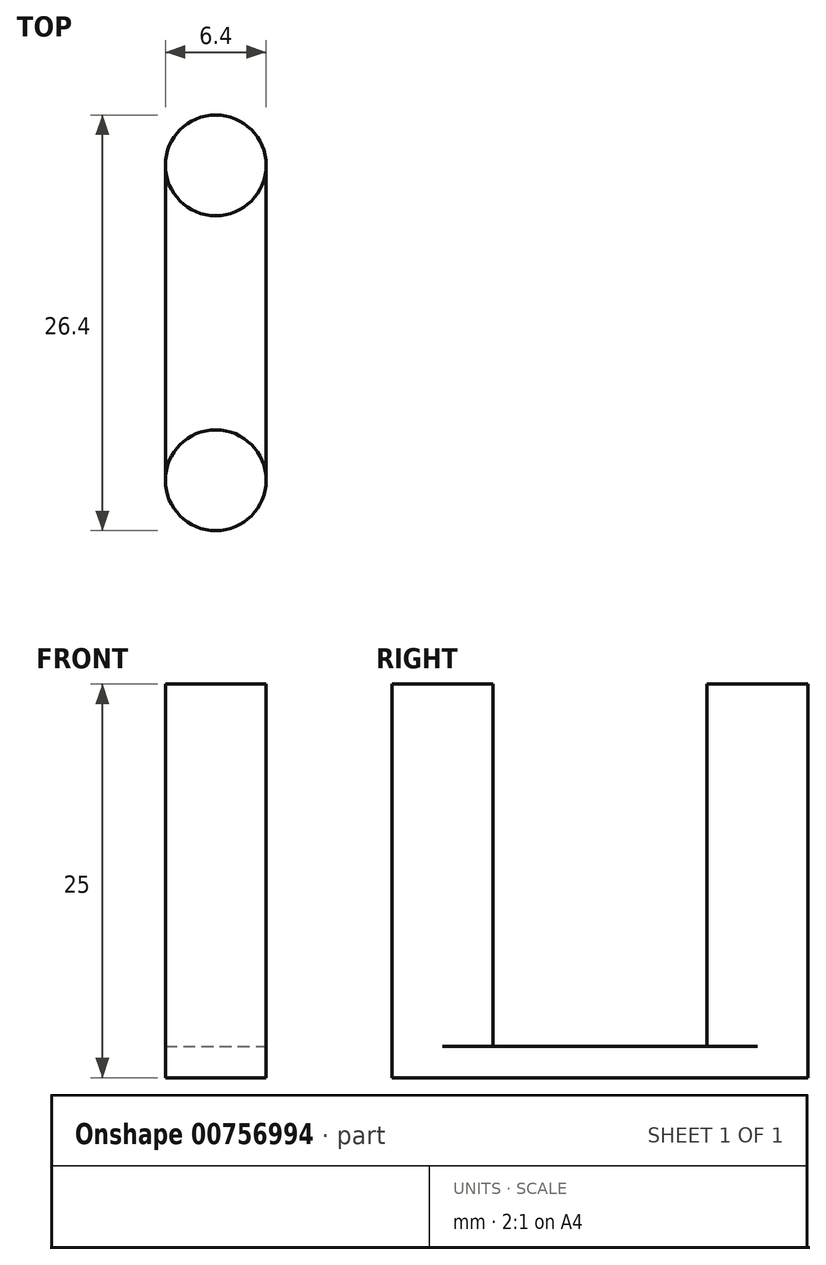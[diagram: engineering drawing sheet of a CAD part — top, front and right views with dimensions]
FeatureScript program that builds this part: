
annotation { "Feature Type Name" : "Feature", "Feature Type Description" : "" }
export const myFeature = defineFeature(function(context is Context, id is Id, definition is map)
    precondition{}
    {
        {
            var Q0;
            Q0=qCreatedBy(makeId("Top.planeOp"),FACE);
            var sketch = newSketch(context, id + "F0", { "sketchPlane" : qUnion([Q0])});
            skCircle(sketch, "E0", {"center": v(0, 0) * mm, "radius": 3.2 * mm});
            skPoint(sketch, "E0.centerSnap0", {"position": v(0, 0) * mm});
            skCircle(sketch, "E1", {"center": v(0, -20) * mm, "radius": 3.2 * mm});
            skLineSegment(sketch, "E2", {"start": v(0, 0) * mm, "end": v(0, -20) * mm, "construction": true});
            skLineSegment(sketch, "E3", {"start": v(3.2, -20) * mm, "end": v(3.2, 0) * mm});
            skLineSegment(sketch, "E4", {"start": v(-3.2, -20) * mm, "end": v(-3.2, 0) * mm});
            skPoint(sketch, "E5.start.orphan", {"position": v(0, -10) * mm});
            skSolve(sketch);
        }
        {
            var Q0;
            {var subQ0=sQuery(id+"F0.wireOp",EDGE,"E1");var subQ1=makeQuery(id+"F0.imprint","INTERSECT",VERTEX,{"derivedFrom":[subQ0,sQuery(id+"F0.wireOp",EDGE,"E3")]});Q0=makeQuery(id+"F0.imprint","IMPRINT",FACE,{"disambiguationData":[TD([[makeQuery(id+"F0.imprint","IMPRINT",EDGE,{"disambiguationData":[TD([[subQ1,-1.0]])],"derivedFrom":subQ0}),1.0]])]});}
            var Q1;
            {var subQ0=sQuery(id+"F0.wireOp",EDGE,"E0");var subQ1=makeQuery(id+"F0.imprint","INTERSECT",VERTEX,{"derivedFrom":[subQ0,sQuery(id+"F0.wireOp",EDGE,"E3")]});Q1=makeQuery(id+"F0.imprint","IMPRINT",FACE,{"disambiguationData":[TD([[makeQuery(id+"F0.imprint","IMPRINT",EDGE,{"disambiguationData":[TD([[subQ1,-1.0]])],"derivedFrom":subQ0}),1.0]])]});}
            extrude(context, id + "F1", {"entities" : qUnion([Q0, Q1]), "depth" : 25 * mm, "offsetDistance" : 25 * mm});
        }
        {
            var Q0;
            {var subQ0=sQuery(id+"F0.wireOp",EDGE,"E3");Q0=makeQuery(id+"F0.imprint","IMPRINT",FACE,{"disambiguationData":[TD([[makeQuery(id+"F0.imprint","IMPRINT",EDGE,{"derivedFrom":subQ0}),1.0]])]});}
            extrude(context, id + "F2", {"entities" : qUnion([Q0]), "operationType" : NewBodyOperationType.ADD, "depth" : 2 * mm, "offsetDistance" : 25 * mm});
        }
    });
